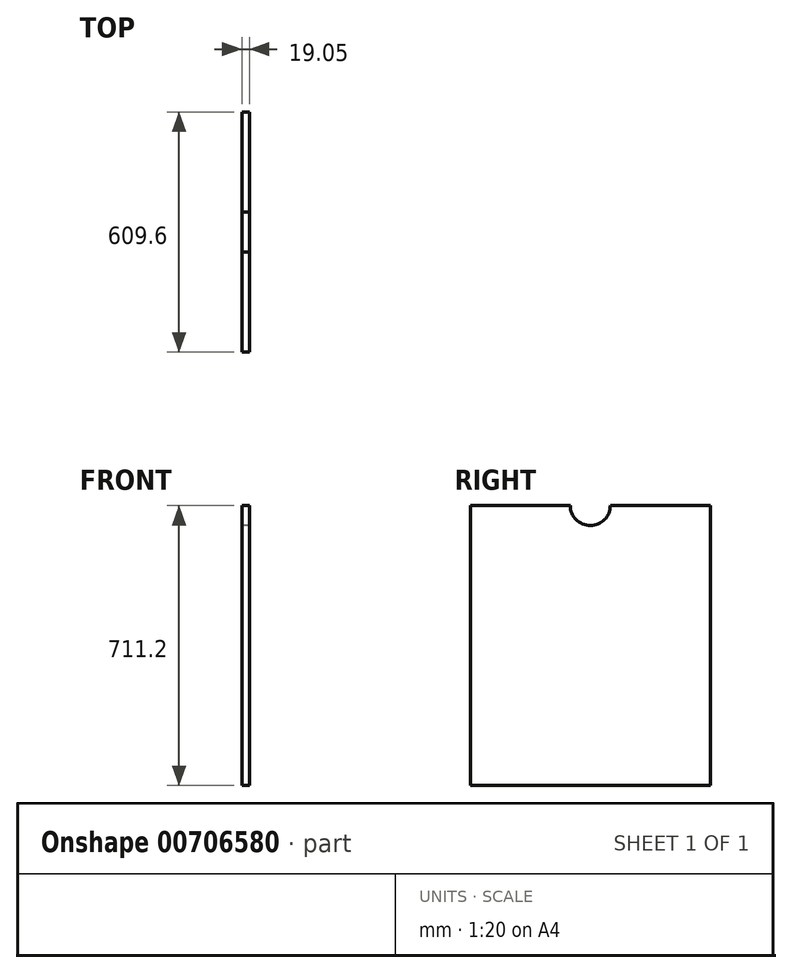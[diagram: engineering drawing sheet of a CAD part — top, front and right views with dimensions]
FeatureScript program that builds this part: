
annotation { "Feature Type Name" : "Feature", "Feature Type Description" : "" }
export const myFeature = defineFeature(function(context is Context, id is Id, definition is map)
    precondition{}
    {
        {
            var Q0;
            Q0=qCreatedBy(makeId("Right.planeOp"),FACE);
            var sketch = newSketch(context, id + "F0", { "sketchPlane" : qUnion([Q0])});
            skLineSegment(sketch, "E0.bottom", {"start": v(304.8, 355.6) * mm, "end": v(-304.8, 355.6) * mm});
            skLineSegment(sketch, "E0.top", {"start": v(304.8, -355.6) * mm, "end": v(-304.8, -355.6) * mm});
            skLineSegment(sketch, "E0.left", {"start": v(304.8, 355.6) * mm, "end": v(304.8, -355.6) * mm});
            skLineSegment(sketch, "E0.right", {"start": v(-304.8, 355.6) * mm, "end": v(-304.8, -355.6) * mm});
            skPoint(sketch, "E0.middle", {"position": v(0, 0) * mm});
            skCircle(sketch, "E1", {"center": v(0, 355.6) * mm, "radius": 50.8 * mm});
            skSolve(sketch);
        }
        {
            var Q0;
            Q0=makeQuery(id+"F0.imprint","IMPRINT",FACE,{"disambiguationData":[TD([[makeQuery(id+"F0.imprint","IMPRINT",EDGE,{"derivedFrom":sQuery(id+"F0.wireOp",EDGE,"E0.top")}),-1.0]])]});
            extrude(context, id + "F1", {"entities" : qUnion([Q0]), "depth" : 19.05 * mm, "offsetDistance" : 25.4 * mm});
        }
    });
